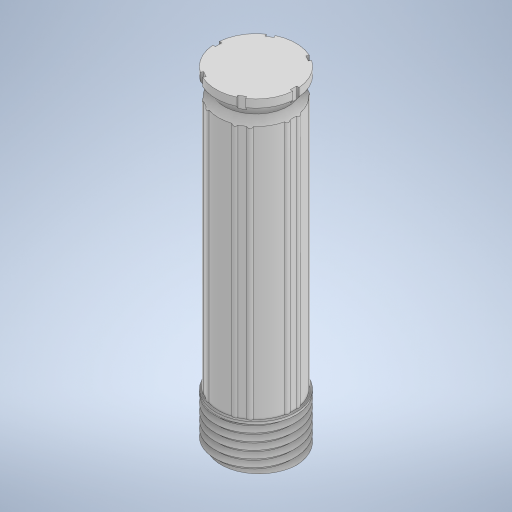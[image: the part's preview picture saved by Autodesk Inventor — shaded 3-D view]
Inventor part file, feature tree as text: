
AUTODESK INVENTOR PART (.ipt)
format: ipt  version: 2024 (Build 280153000, 153)  size: 527,360 bytes
history: native  units: mm
features: sketch x7, extrude x5, pattern_circular x2, other x1, revolve x1, fillet x1
ambient origin geometry x8: Origin, YZ Plane, XZ Plane, XY Plane, X Axis, Y Axis, Z Axis, Center Point
bodies: Volumenkörper1 (feature_tree)
feature tree (17):
  extrude  "Extrusion1"  Depth=61.0mm TaperAngle=0.0deg
  other  "Spirale1"
  extrude  "Extrusion9"  Depth=3.5mm
  revolve  "Umdrehung1"
  extrude  "Extrusion6"  Depth=2.0mm
  pattern_circular  "Runde Anordnung1"  Count=4  [1 undecoded]
  extrude  "Extrusion7"  Depth=0.65mm TaperAngle=360.0deg
  pattern_circular  "Runde Anordnung2"  [2 undecoded]
  extrude  "Extrusion10"  Depth=0.65mm TaperAngle=0.0deg
  fillet  "Rundung6"  Radius=60.0mm
  sketch  "Skizze1"  dims[d0=15.0mm d1=61.0mm d2=0.0mm]
  sketch  "Skizze6"  dims[d20=1.5mm d21=3.5mm]
  sketch  "Skizze8"  dims[d22=2.0mm d23=2.0mm]
  sketch  "Skizze9"  dims[d24=90.0deg]
  sketch  "Skizze12"  dims[d32=0.5mm]
  sketch  "Skizze14"  dims[d33=0.6mm]
  sketch  "Skizze15"  dims[d34=0.6mm d35=40.0mm d36=21.85mm d37=0.0mm d38=0.0mm d39=60.0mm d40=360.0deg d42=1.0mm d43=27.0mm d44=21.85mm d45=0.0mm d46=0.0mm d47=60.0mm d48=360.0deg d51=1.0mm d54=15.0mm d56=1.4mm d58=1.4mm d59=9.85mm d60=10.0mm d61=0.0mm d62=90.0deg d63=90.0deg d64=0.0mm d65=0.0mm d68=15.0mm d69=52.8mm d70=0.0mm d71=60.0deg d72=0.2mm d73=7.5mm d74=15.0mm d75=14.5mm d76=15.0mm d77=27.0mm d78=21.85mm d79=0.0mm d80=0.0mm d82=0.65mm d52=0.0mm d53=0.0mm d55=0.0mm]
note: 3 required parameter values undecoded (feature->parameter linkage not recoverable at this tier; creation-order binding heuristic only, values carry confidence <= 0.55)
